# Revit family: Maxlogic  bouton de démarrage d'extinction
name_source: partatom
category: Fire Alarm Devices
units: mm (PartAtom-declared; Revit-internal decimal feet)

## family parameters
Cut with Voids When Loaded = No
Host = Face
Maintain Annotation Orientation = Yes
OmniClass Number = 23.85.30.21
OmniClass Title = Environmental Detection/Registration
Part Type = Normal
Room Calculation Point = No
Round Connector Dimension = Use Diameter
Shared = No

## types (1)
- Maxlogic bouton de démarrage d'extinction
    Adresse ligne 1 = Şerifali Mahallesi Kutup Sokak No:27/1-2-4 Ümraniye TR-34775 İSTANBUL
    Code de  Performance = EN 12094-3
    Code de Produit = ML-2710.MR
    Cost = 0 $
    Couleur = Jaune
    Couvercle de protection = ML-0710
    Default Elevation = 0 mm  [stored 0 ft]
    Description = bouton de démarrage d'extinction
    Deuxime Matèriel = Plastique
    Durée de la garantie Travail = 2
    Durée de la garantie réservé = 2
    Hauteur Nominale = 91 mm
    Hauteur de Montage = Hauteur  1,4m du sol (+/-200mm)
    Largeur Nominale = 58 mm
    Longeur Nominale = 87 mm
    Manuel d'installation = https://mavilielektronik.com
    Manufacturer = Mavili Elektronik Ticaret A.Ş.
    Matériel Principe = Plastique Jaune ABS
    Model = MaxLogic
    Numèro de Fax = (+)90 216 466 45 10
    Numéro de pose des travaux publics = 833-260
    Poids = 140 gr.
    Surface de Montage = Montage à mur
    Tempèrature de Fonctionnement = (-10°C) - (+55°C)
    URL = https://www.mavili.com.tr
    Unité de durée de garantie = Year
    Voltage de fonctionnement (default) = 24 V/DC
    protection de Classe = IP22D
    voltage fonction d'opération = 10-30 V/DC

note: [stored X ft] marks values corroborated as IEEE doubles in the binary element streams (Revit-internal decimal feet)

## geometry (parser evidence)
native form markers: Sweep x3
no freeform markers — native parametric forms only
